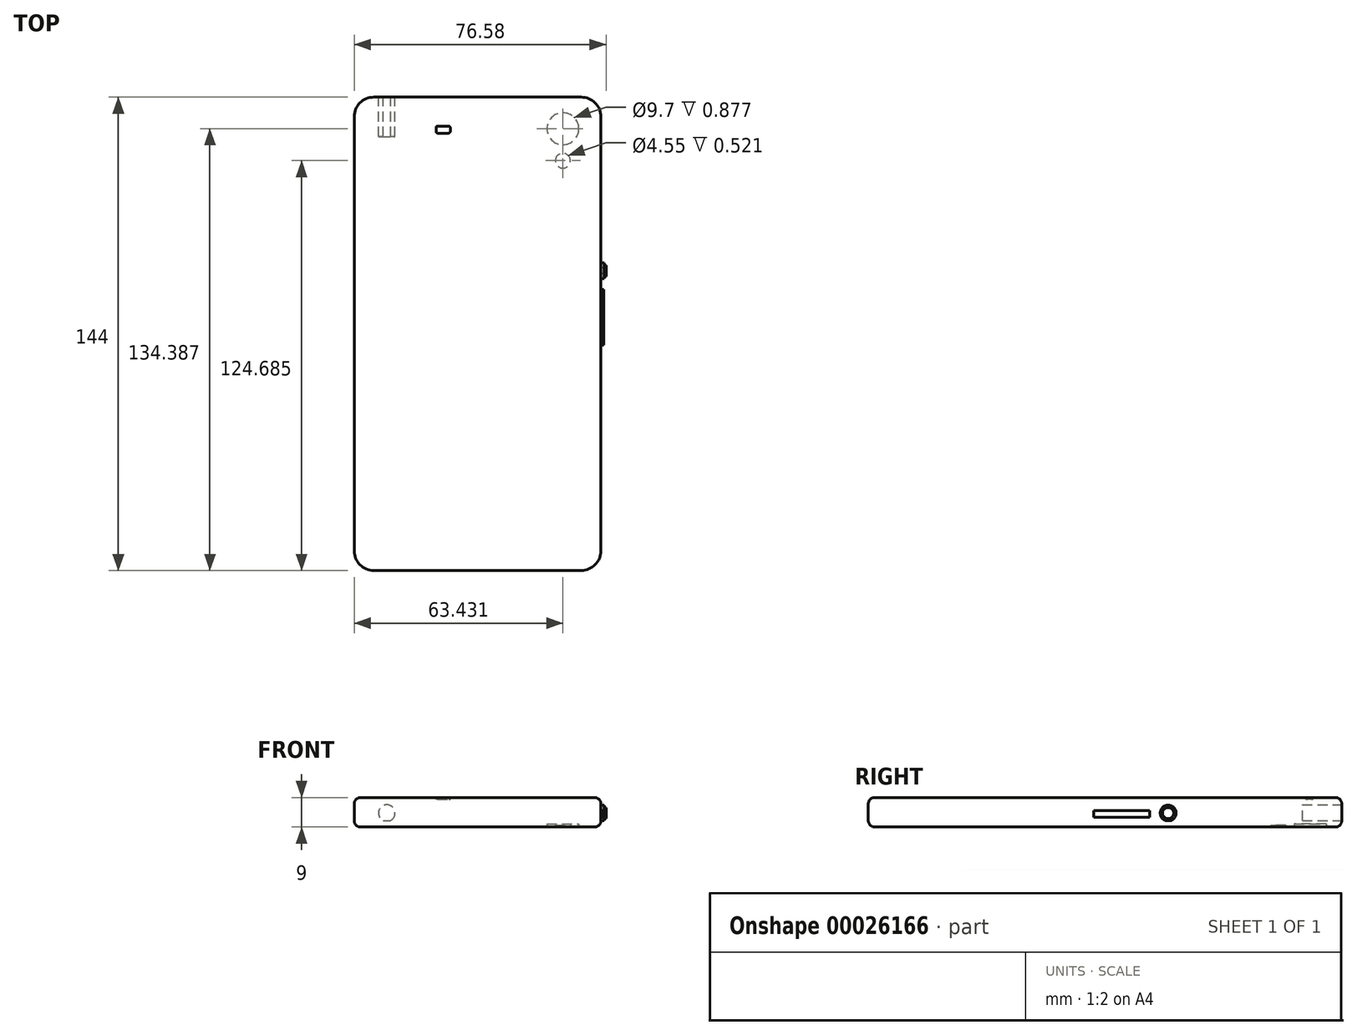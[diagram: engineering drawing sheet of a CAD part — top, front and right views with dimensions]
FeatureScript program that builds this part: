
annotation { "Feature Type Name" : "Feature", "Feature Type Description" : "" }
export const myFeature = defineFeature(function(context is Context, id is Id, definition is map)
    precondition{}
    {
        {
            var Q0;
            Q0=qCreatedBy(makeId("Top.planeOp"),FACE);
            var sketch = newSketch(context, id + "F0", { "sketchPlane" : qUnion([Q0])});
            skLineSegment(sketch, "E0.bottom", {"start": v(-48.3, -67.64) * mm, "end": v(26.7, -67.64) * mm});
            skLineSegment(sketch, "E0.top", {"start": v(-48.3, 76.36) * mm, "end": v(26.7, 76.36) * mm});
            skLineSegment(sketch, "E0.left", {"start": v(-48.3, -67.64) * mm, "end": v(-48.3, 76.36) * mm});
            skLineSegment(sketch, "E0.right", {"start": v(26.7, -67.64) * mm, "end": v(26.7, 76.36) * mm});
            skSolve(sketch);
        }
        {
            var Q0;
            Q0=makeQuery(id+"F0.imprint","IMPRINT",FACE,{"disambiguationData":[TD([[makeQuery(id+"F0.imprint","IMPRINT",EDGE,{"derivedFrom":sQuery(id+"F0.wireOp",EDGE,"E0.bottom")}),1.0]])]});
            extrude(context, id + "F1", {"entities" : qUnion([Q0]), "depth" : 9 * mm});
        }
        {
            var Q0;
            Q0=makeQuery(id+"F1.opExtrude","SWEPT_EDGE",EDGE,{"disambiguationData":[OSD([sQuery(id+"F0.wireOp",EDGE,"E0.bottom"),sQuery(id+"F0.wireOp",EDGE,"E0.right")])]});
            var Q1;
            Q1=makeQuery(id+"F1.opExtrude","SWEPT_EDGE",EDGE,{"disambiguationData":[OSD([sQuery(id+"F0.wireOp",EDGE,"E0.top"),sQuery(id+"F0.wireOp",EDGE,"E0.right")])]});
            var Q2;
            Q2=makeQuery(id+"F1.opExtrude","SWEPT_EDGE",EDGE,{"disambiguationData":[OSD([sQuery(id+"F0.wireOp",EDGE,"E0.bottom"),sQuery(id+"F0.wireOp",EDGE,"E0.left")])]});
            var Q3;
            Q3=makeQuery(id+"F1.opExtrude","SWEPT_EDGE",EDGE,{"disambiguationData":[OSD([sQuery(id+"F0.wireOp",EDGE,"E0.top"),sQuery(id+"F0.wireOp",EDGE,"E0.left")])]});
            fillet(context, id + "F2", {"entities" : qUnion([Q0, Q1, Q2, Q3]), "radius" : 6 * mm, "tangentPropagation" : true, "allowEdgeOverflow" : false});
        }
        {
            var Q0;
            Q0=makeQuery(id+"F1.opExtrude","CAP_EDGE",EDGE,{"disambiguationData":[OSD([sQuery(id+"F0.wireOp",EDGE,"E0.left")])],"isStart":false});
            fillet(context, id + "F3", {"entities" : qUnion([Q0]), "radius" : 2 * mm, "tangentPropagation" : true, "allowEdgeOverflow" : false});
        }
        {
            var Q0;
            Q0=makeQuery(id+"F1.opExtrude","CAP_EDGE",EDGE,{"disambiguationData":[OSD([sQuery(id+"F0.wireOp",EDGE,"E0.bottom")])],"isStart":true});
            fillet(context, id + "F4", {"entities" : qUnion([Q0]), "radius" : 2 * mm, "tangentPropagation" : true, "allowEdgeOverflow" : false});
        }
        {
            var Q0;
            Q0=makeQuery(id+"F1.opExtrude","SWEPT_FACE",FACE,{"disambiguationData":[OSD([sQuery(id+"F0.wireOp",EDGE,"E0.top")])]});
            var sketch = newSketch(context, id + "F5", { "sketchPlane" : qUnion([Q0])});
            skCircle(sketch, "E1", {"center": v(38.4, 4.25) * mm, "radius": 2.52 * mm});
            skSolve(sketch);
        }
        {
            var Q0;
            {var subQ0=sQuery(id+"F0.wireOp",EDGE,"E0.top");var subQ1=makeQuery(id+"F4.opFillet","BLEND_EDGE",EDGE,{"blendedFrom":[makeQuery(id+"F1.opExtrude","CAP_EDGE",EDGE,{"disambiguationData":[OSD([subQ0])],"isStart":true}),makeQuery(id+"F1.opExtrude","SWEPT_FACE",FACE,{"disambiguationData":[OSD([subQ0])]})],"blendedInto":[makeQuery(id+"F1.opExtrude","SWEPT_FACE",FACE,{"disambiguationData":[OSD([subQ0])]})]});var subQ2=sQuery(id+"F5.wireOp",EDGE,"E1");var subQ4=makeQuery(id+"F5.imprint","INTERSECT",VERTEX,{"disambiguationData":[OD(0.0)],"derivedFrom":[subQ1,subQ2]});Q0=makeQuery(id+"F5.imprint","IMPRINT",FACE,{"disambiguationData":[TD([[makeQuery(id+"F5.imprint","IMPRINT",EDGE,{"disambiguationData":[TD([[subQ4,-1.0]])],"derivedFrom":subQ2}),1.0]])]});}
            extrude(context, id + "F6", {"entities" : qUnion([Q0]), "operationType" : NewBodyOperationType.REMOVE, "oppositeDirection" : true, "depth" : 12 * mm});
        }
        {
            var Q0;
            Q0=makeQuery(id+"F1.opExtrude","SWEPT_FACE",FACE,{"disambiguationData":[OSD([sQuery(id+"F0.wireOp",EDGE,"E0.right")])]});
            var sketch = newSketch(context, id + "F7", { "sketchPlane" : qUnion([Q0])});
            skCircle(sketch, "E2", {"center": v(23.54, 4.24) * mm, "radius": 2.42 * mm});
            skCircle(sketch, "E3", {"center": v(23.54, 4.24) * mm, "radius": 1.7 * mm});
            skSolve(sketch);
        }
        {
            var Q0;
            Q0=makeQuery(id+"F7.imprint","IMPRINT",FACE,{"disambiguationData":[TD([[makeQuery(id+"F7.imprint","IMPRINT",EDGE,{"derivedFrom":sQuery(id+"F7.wireOp",EDGE,"E3")}),-1.0]])]});
            extrude(context, id + "F8", {"entities" : qUnion([Q0]), "operationType" : NewBodyOperationType.ADD, "depth" : 1 * mm});
        }
        {
            var Q0;
            Q0=makeQuery(id+"F8.boolean.opBoolean","SPLIT",FACE,{"disambiguationData":[TD([makeQuery(id+"F8.opExtrude","SWEPT_FACE",FACE,{"disambiguationData":[OSD([sQuery(id+"F7.wireOp",EDGE,"E3")])]})])],"derivedFrom":makeQuery(id+"F1.opExtrude","SWEPT_FACE",FACE,{"disambiguationData":[OSD([sQuery(id+"F0.wireOp",EDGE,"E0.right")])]})});
            extrude(context, id + "F9", {"entities" : qUnion([Q0]), "operationType" : NewBodyOperationType.ADD, "depth" : 1.57 * mm});
        }
        {
            var Q0;
            {var subQ0=sQuery(id+"F0.wireOp",EDGE,"E0.right");Q0=makeQuery(id+"F8.boolean.opBoolean","SPLIT",FACE,{"disambiguationData":[TD([makeQuery(id+"F3.opFillet","BLEND_FACE",FACE,{"disambiguationData":[OSD([subQ0])]})])],"derivedFrom":makeQuery(id+"F1.opExtrude","SWEPT_FACE",FACE,{"disambiguationData":[OSD([subQ0])]})});}
            var sketch = newSketch(context, id + "F10", { "sketchPlane" : qUnion([Q0])});
            skLineSegment(sketch, "E4.bottom", {"start": v(17.9, 4.94) * mm, "end": v(0.9, 4.94) * mm});
            skLineSegment(sketch, "E4.top", {"start": v(17.9, 2.94) * mm, "end": v(0.9, 2.94) * mm});
            skLineSegment(sketch, "E4.left", {"start": v(17.9, 4.94) * mm, "end": v(17.9, 2.94) * mm});
            skLineSegment(sketch, "E4.right", {"start": v(0.9, 4.94) * mm, "end": v(0.9, 2.94) * mm});
            skSolve(sketch);
        }
        {
            var Q0;
            Q0=makeQuery(id+"F10.imprint","IMPRINT",FACE,{"disambiguationData":[TD([[makeQuery(id+"F10.imprint","IMPRINT",EDGE,{"derivedFrom":sQuery(id+"F10.wireOp",EDGE,"E4.bottom")}),1.0]])]});
            extrude(context, id + "F11", {"entities" : qUnion([Q0]), "operationType" : NewBodyOperationType.ADD, "depth" : 0.82 * mm});
        }
        {
            var Q0;
            Q0=makeQuery(id+"F1.opExtrude","CAP_FACE",FACE,{"disambiguationData":[OSD([sQuery(id+"F0.wireOp",EDGE,"E0.bottom"),sQuery(id+"F0.wireOp",EDGE,"E0.top"),sQuery(id+"F0.wireOp",EDGE,"E0.left"),sQuery(id+"F0.wireOp",EDGE,"E0.right")])],"isStart":true});
            var sketch = newSketch(context, id + "F12", { "sketchPlane" : qUnion([Q0])});
            skCircle(sketch, "E5", {"center": v(15.13, -66.75) * mm, "radius": 4.85 * mm});
            skSolve(sketch);
        }
        {
            var Q0;
            Q0=makeQuery(id+"F12.imprint","IMPRINT",FACE,{"disambiguationData":[TD([[makeQuery(id+"F12.imprint","IMPRINT",EDGE,{"derivedFrom":sQuery(id+"F12.wireOp",EDGE,"E5")}),1.0]])]});
            extrude(context, id + "F13", {"entities" : qUnion([Q0]), "operationType" : NewBodyOperationType.REMOVE, "oppositeDirection" : true, "depth" : 0.88 * mm});
        }
        {
            var Q0;
            Q0=makeQuery(id+"F1.opExtrude","CAP_FACE",FACE,{"disambiguationData":[OSD([sQuery(id+"F0.wireOp",EDGE,"E0.bottom"),sQuery(id+"F0.wireOp",EDGE,"E0.top"),sQuery(id+"F0.wireOp",EDGE,"E0.left"),sQuery(id+"F0.wireOp",EDGE,"E0.right")])],"isStart":true});
            var sketch = newSketch(context, id + "F14", { "sketchPlane" : qUnion([Q0])});
            skCircle(sketch, "E6", {"center": v(15.13, -57.05) * mm, "radius": 2.28 * mm});
            skSolve(sketch);
        }
        {
            var Q0;
            Q0=makeQuery(id+"F14.imprint","IMPRINT",FACE,{"disambiguationData":[TD([[makeQuery(id+"F14.imprint","IMPRINT",EDGE,{"derivedFrom":sQuery(id+"F14.wireOp",EDGE,"E6")}),1.0]])]});
            extrude(context, id + "F15", {"entities" : qUnion([Q0]), "operationType" : NewBodyOperationType.REMOVE, "oppositeDirection" : true, "depth" : 0.52 * mm});
        }
        {
            var Q0;
            Q0=makeQuery(id+"F1.opExtrude","CAP_FACE",FACE,{"disambiguationData":[OSD([sQuery(id+"F0.wireOp",EDGE,"E0.bottom"),sQuery(id+"F0.wireOp",EDGE,"E0.top"),sQuery(id+"F0.wireOp",EDGE,"E0.left"),sQuery(id+"F0.wireOp",EDGE,"E0.right")])],"isStart":false});
            var sketch = newSketch(context, id + "F16", { "sketchPlane" : qUnion([Q0])});
            skLineSegment(sketch, "E7.bottom", {"start": v(-44.25, 59.46) * mm, "end": v(22.48, 59.46) * mm});
            skLineSegment(sketch, "E7.top", {"start": v(-44.25, -61.64) * mm, "end": v(22.48, -61.64) * mm});
            skLineSegment(sketch, "E7.left", {"start": v(-44.25, 59.46) * mm, "end": v(-44.25, -61.64) * mm});
            skLineSegment(sketch, "E7.right", {"start": v(22.48, 59.46) * mm, "end": v(22.48, -61.64) * mm});
            skSolve(sketch);
        }
        {
            var Q0;
            Q0=makeQuery(id+"F16.imprint","IMPRINT",FACE,{"disambiguationData":[TD([[makeQuery(id+"F16.imprint","IMPRINT",EDGE,{"derivedFrom":sQuery(id+"F16.wireOp",EDGE,"E7.bottom")}),1.0]])]});
            var sketch = newSketch(context, id + "F17", { "sketchPlane" : qUnion([Q0])});
            skLineSegment(sketch, "E8.bottom", {"start": v(-23.42, 67.57) * mm, "end": v(-19.1, 67.57) * mm});
            skLineSegment(sketch, "E8.top", {"start": v(-23.42, 65.4) * mm, "end": v(-19.1, 65.4) * mm});
            skLineSegment(sketch, "E8.left", {"start": v(-23.42, 67.57) * mm, "end": v(-23.42, 65.4) * mm});
            skLineSegment(sketch, "E8.right", {"start": v(-19.1, 67.57) * mm, "end": v(-19.1, 65.4) * mm});
            skSolve(sketch);
        }
        {
            var Q0;
            Q0=makeQuery(id+"F17.imprint","IMPRINT",FACE,{"disambiguationData":[TD([[makeQuery(id+"F17.imprint","IMPRINT",EDGE,{"derivedFrom":sQuery(id+"F17.wireOp",EDGE,"E8.bottom")}),-1.0]])]});
            extrude(context, id + "F18", {"entities" : qUnion([Q0]), "operationType" : NewBodyOperationType.ADD, "depth" : 7.1 * mm});
        }
        {
            var Q0;
            Q0=makeQuery(id+"F18.opExtrude","SWEPT_EDGE",EDGE,{"disambiguationData":[OSD([sQuery(id+"F17.wireOp",EDGE,"E8.bottom"),sQuery(id+"F17.wireOp",EDGE,"E8.left")])]});
            var Q1;
            Q1=makeQuery(id+"F18.opExtrude","SWEPT_EDGE",EDGE,{"disambiguationData":[OSD([sQuery(id+"F17.wireOp",EDGE,"E8.top"),sQuery(id+"F17.wireOp",EDGE,"E8.left")])]});
            var Q2;
            Q2=makeQuery(id+"F18.opExtrude","SWEPT_EDGE",EDGE,{"disambiguationData":[OSD([sQuery(id+"F17.wireOp",EDGE,"E8.bottom"),sQuery(id+"F17.wireOp",EDGE,"E8.right")])]});
            var Q3;
            Q3=makeQuery(id+"F18.opExtrude","SWEPT_EDGE",EDGE,{"disambiguationData":[OSD([sQuery(id+"F17.wireOp",EDGE,"E8.top"),sQuery(id+"F17.wireOp",EDGE,"E8.right")])]});
            fillet(context, id + "F19", {"entities" : qUnion([Q0, Q1, Q2, Q3]), "radius" : 0.5 * mm, "tangentPropagation" : true, "allowEdgeOverflow" : false});
        }
        {
            var Q0;
            Q0=makeQuery(id+"F18.opExtrude","CAP_FACE",FACE,{"disambiguationData":[OSD([sQuery(id+"F17.wireOp",EDGE,"E8.bottom"),sQuery(id+"F17.wireOp",EDGE,"E8.top"),sQuery(id+"F17.wireOp",EDGE,"E8.left"),sQuery(id+"F17.wireOp",EDGE,"E8.right")])],"isStart":false});
            extrude(context, id + "F20", {"entities" : qUnion([Q0]), "operationType" : NewBodyOperationType.REMOVE, "oppositeDirection" : true, "depth" : 7.64 * mm});
        }
    });
